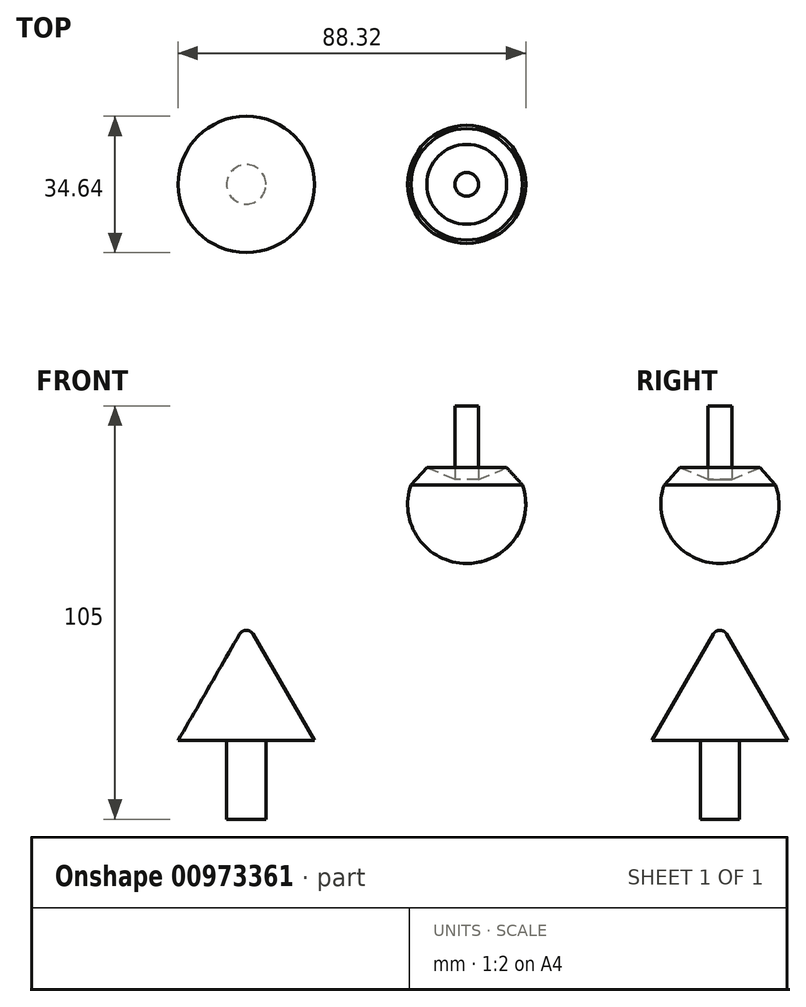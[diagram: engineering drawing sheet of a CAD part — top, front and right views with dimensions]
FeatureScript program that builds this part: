
annotation { "Feature Type Name" : "Feature", "Feature Type Description" : "" }
export const myFeature = defineFeature(function(context is Context, id is Id, definition is map)
    precondition{}
    {
        {
            var Q0;
            Q0=qCreatedBy(makeId("Top.planeOp"),FACE);
            cPlane(context, id + "F0", {"entities" : qUnion([Q0]), "cplaneType" : CPlaneType.OFFSET, "offset" : 5 * mm, "width" : 150 * mm, "height" : 150 * mm});
        }
        {
            var Q0;
            Q0=qCreatedBy(makeId("Front.planeOp"),FACE);
            var sketch = newSketch(context, id + "F1", { "sketchPlane" : qUnion([Q0])});
            skLineSegment(sketch, "E0", {"start": v(0, 5) * mm, "end": v(0, -15) * mm});
            skArc(sketch, "E1", {"start": v(6.14, 13.69) * mm, "mid": v(14.67, -3.14) * mm, "end": v(0, -15) * mm});
            skLineSegment(sketch, "E2", {"start": v(0, 15) * mm, "end": v(0, 5) * mm});
            skLineSegment(sketch, "E3", {"start": v(0, 5) * mm, "end": v(14.14, 5) * mm});
            skLineSegment(sketch, "E4", {"start": v(0, 5) * mm, "end": v(6.14, 13.69) * mm});
            skPoint(sketch, "E5.orphan", {"position": v(7.07, 15) * mm});
            skLineSegment(sketch, "E6", {"start": v(6.14, 13.69) * mm, "end": v(14.14, 5) * mm});
            skLineSegment(sketch, "E7", {"start": v(0, 5) * mm, "end": v(10.14, 9.34) * mm});
            skLineSegment(sketch, "E8", {"start": v(10.14, 9.34) * mm, "end": v(13.84, 11.08) * mm});
            skSolve(sketch);
        }
        {
            var Q0;
            {var subQ0=sQuery(id+"F1.wireOp",EDGE,"E0");Q0=makeQuery(id+"F1.imprint","IMPRINT",FACE,{"disambiguationData":[TD([[makeQuery(id+"F1.imprint","IMPRINT",EDGE,{"derivedFrom":subQ0}),1.0]])]});}
            var Q1;
            {var subQ1=sQuery(id+"F1.wireOp",EDGE,"E1");var subQ3=sQuery(id+"F1.wireOp",EDGE,"E8");var subQ4=makeQuery(id+"F1.imprint","INTERSECT",VERTEX,{"derivedFrom":[subQ1,subQ3]});Q1=makeQuery(id+"F1.imprint","IMPRINT",FACE,{"disambiguationData":[TD([[makeQuery(id+"F1.imprint","IMPRINT",EDGE,{"disambiguationData":[TD([[subQ4,-1.0]])],"derivedFrom":subQ1}),-1.0]])]});}
            var Q2;
            {var subQ0=sQuery(id+"F1.wireOp",EDGE,"E3");Q2=makeQuery(id+"F1.imprint","IMPRINT",FACE,{"disambiguationData":[TD([[makeQuery(id+"F1.imprint","IMPRINT",EDGE,{"derivedFrom":subQ0}),1.0]])]});}
            var Q3;
            Q3=sQuery(id+"F1.wireOp",EDGE,"E0");
            revolve(context, id + "F2", {"surfaceOperationType" : NewSurfaceOperationType.NEW, "entities" : qUnion([Q0, Q1, Q2]), "axis" : qUnion([Q3]), "revolveType" : RevolveType.FULL});
        }
        {
            var Q0;
            Q0=qCreatedBy(id+"F0.planeOp",FACE);
            var sketch = newSketch(context, id + "F3", { "sketchPlane" : qUnion([Q0])});
            skCircle(sketch, "E9", {"center": v(0, 0) * mm, "radius": 3 * mm});
            skSolve(sketch);
        }
        {
            var Q0;
            Q0 = qSketchRegion(id + "F3", true);
            extrude(context, id + "F4", {"entities" : qUnion([Q0]), "operationType" : NewBodyOperationType.ADD, "depth" : 20 * mm, "offsetDistance" : 25 * mm});
        }
        {
            var Q0;
            Q0=makeQuery(id+"F2.opRevolve","SWEPT_BODY",BODY,{"disambiguationData":[OSD([sQuery(id+"F1.wireOp",EDGE,"E0"),sQuery(id+"F1.wireOp",EDGE,"E1"),sQuery(id+"F1.wireOp",EDGE,"E7"),sQuery(id+"F1.wireOp",EDGE,"E8")])]});
            transform(context, id + "F5", {"entities" : qUnion([Q0]), "transformType" : TransformType.TRANSLATION_3D, "dx" : 56 * mm, "dy" : 0 * mm, "dz" : 50 * mm, "makeCopy" : false});
        }
        {
            var Q0;
            Q0=qCreatedBy(makeId("Front.planeOp"),FACE);
            var sketch = newSketch(context, id + "F6", { "sketchPlane" : qUnion([Q0])});
            skCircle(sketch, "E10.cCircle", {"center": v(0, 0) * mm, "radius": 10 * mm, "construction": true});
            skLineSegment(sketch, "E10.0", {"start": v(17.32, -10) * mm, "end": v(-17.32, -10) * mm});
            skLineSegment(sketch, "E10.1", {"start": v(-17.32, -10) * mm, "end": v(0, 20) * mm});
            skLineSegment(sketch, "E10.2", {"start": v(0, 20) * mm, "end": v(17.32, -10) * mm});
            skPoint(sketch, "E10.0.midPoint", {"position": v(0, -10) * mm});
            skLineSegment(sketch, "E11", {"start": v(0, -10) * mm, "end": v(0, 20) * mm});
            skSolve(sketch);
        }
        {
            var Q0;
            {var subQ0=sQuery(id+"F6.wireOp",EDGE,"E10.1");Q0=makeQuery(id+"F6.imprint","IMPRINT",FACE,{"disambiguationData":[TD([[makeQuery(id+"F6.imprint","IMPRINT",EDGE,{"derivedFrom":subQ0}),-1.0]])]});}
            var Q1;
            Q1=sQuery(id+"F6.wireOp",EDGE,"E11");
            revolve(context, id + "F7", {"surfaceOperationType" : NewSurfaceOperationType.NEW, "entities" : qUnion([Q0]), "axis" : qUnion([Q1]), "revolveType" : RevolveType.FULL});
        }
        {
            var Q0;
            Q0=makeQuery(id+"F7.opRevolve","SWEPT_FACE",FACE,{"disambiguationData":[OSD([sQuery(id+"F6.wireOp",EDGE,"E10.0")])]});
            var sketch = newSketch(context, id + "F8", { "sketchPlane" : qUnion([Q0])});
            skCircle(sketch, "E12", {"center": v(0, 0) * mm, "radius": 5 * mm});
            skSolve(sketch);
        }
        {
            var Q0;
            Q0 = qSketchRegion(id + "F8", true);
            extrude(context, id + "F9", {"entities" : qUnion([Q0]), "operationType" : NewBodyOperationType.ADD, "depth" : 20 * mm, "offsetDistance" : 25 * mm});
        }
        {
            var Q0;
            Q0=qCreatedBy(makeId("Top.planeOp"),FACE);
            cPlane(context, id + "F10", {"entities" : qUnion([Q0]), "cplaneType" : CPlaneType.OFFSET, "offset" : 18 * mm, "width" : 150 * mm, "height" : 150 * mm});
        }
        {
            var Q0;
            Q0=qCreatedBy(id+"F10.planeOp",FACE);
            var sketch = newSketch(context, id + "F11", { "sketchPlane" : qUnion([Q0])});
            skCircle(sketch, "E13", {"center": v(0, 0) * mm, "radius": 1.5 * mm});
            skSolve(sketch);
        }
        {
            var Q0;
            Q0 = qSketchRegion(id + "F11", true);
            extrude(context, id + "F12", {"entities" : qUnion([Q0]), "operationType" : NewBodyOperationType.REMOVE, "depth" : 2 * mm, "offsetDistance" : 25 * mm});
        }
        {
            var Q0;
            Q0=makeQuery(id+"F12.boolean.opBoolean","COPY",FACE,{"derivedFrom":makeQuery(id+"F12.opExtrude","CAP_FACE",FACE,{"disambiguationData":[OSD([sQuery(id+"F11.wireOp",EDGE,"E13")])],"isStart":true})});
            fillet(context, id + "F13", {"entities" : qUnion([Q0]), "tangentPropagation" : true, "radius" : 1.9 * mm, "defaultsChanged" : true, "vertexSettings" : [], "allowEdgeOverflow" : false});
        }
    });
